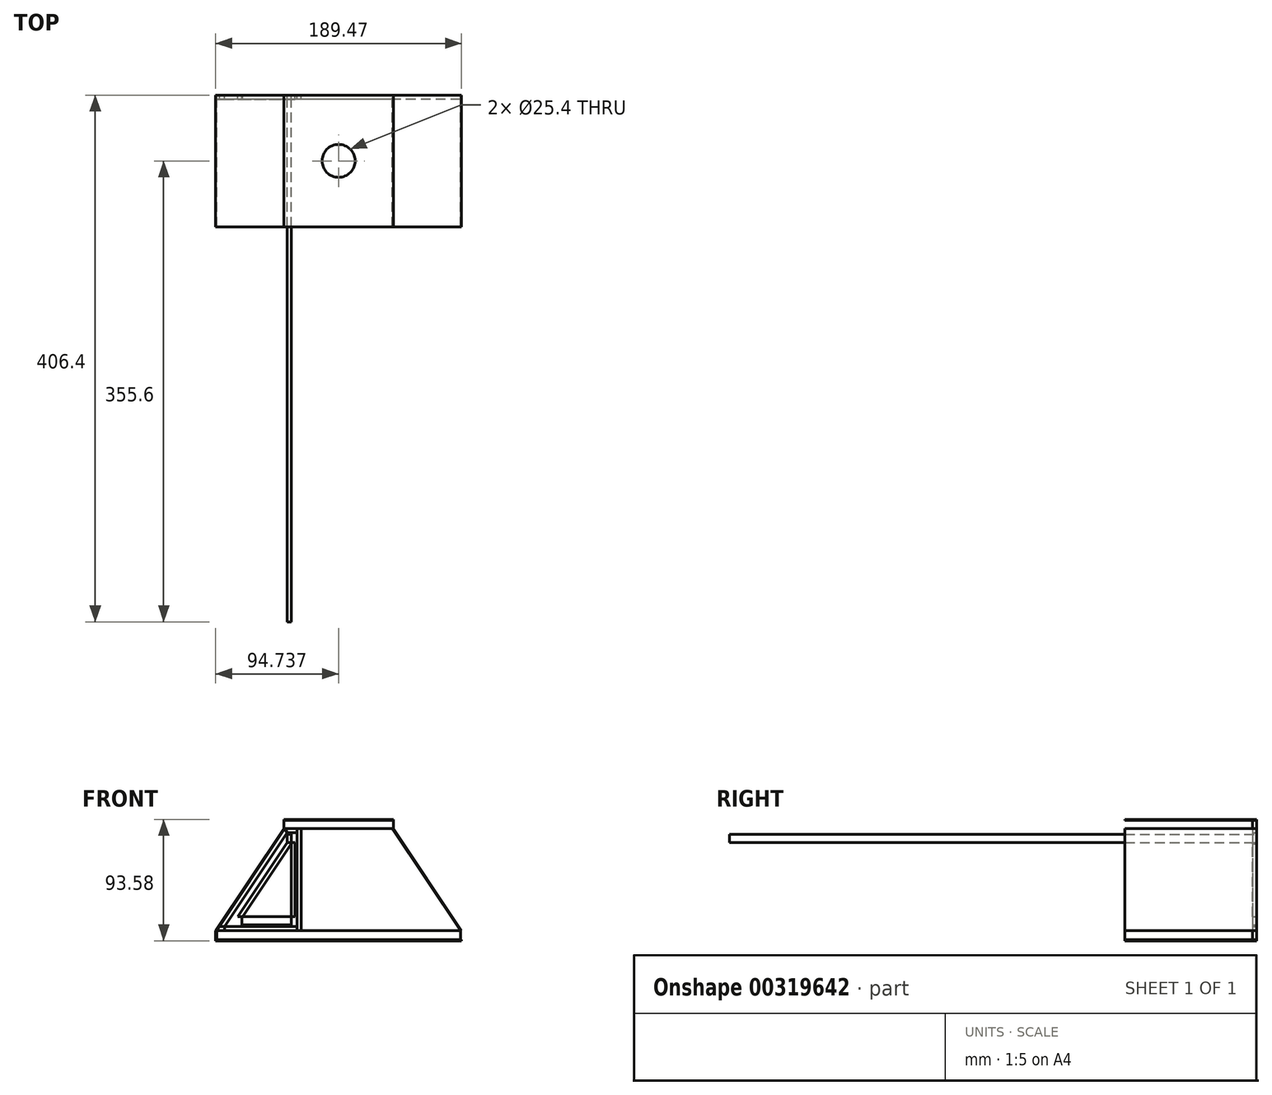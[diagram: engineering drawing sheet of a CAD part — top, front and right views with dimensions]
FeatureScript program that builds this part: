
annotation { "Feature Type Name" : "Feature", "Feature Type Description" : "" }
export const myFeature = defineFeature(function(context is Context, id is Id, definition is map)
    precondition{}
    {
        {
            var Q0;
            Q0=qCreatedBy(makeId("Front.planeOp"),FACE);
            var sketch = newSketch(context, id + "F0", { "sketchPlane" : qUnion([Q0])});
            skLineSegment(sketch, "E0", {"start": v(-44.45, 0) * mm, "end": v(0, 0) * mm});
            skLineSegment(sketch, "E1", {"start": v(0, 0) * mm, "end": v(0, 6.35) * mm});
            skLineSegment(sketch, "E2", {"start": v(-44.45, 6.35) * mm, "end": v(-44.45, 0) * mm});
            skLineSegment(sketch, "E3", {"start": v(-44.45, 6.35) * mm, "end": v(0, 6.35) * mm});
            skLineSegment(sketch, "E4", {"start": v(-41.28, 6.35) * mm, "end": v(-41.28, 0) * mm});
            skLineSegment(sketch, "E5", {"start": v(-3.17, 6.35) * mm, "end": v(-3.17, 0) * mm});
            skLineSegment(sketch, "E6", {"start": v(-3.18, 62.54) * mm, "end": v(-40.63, 6.35) * mm});
            skLineSegment(sketch, "E7", {"start": v(-3.18, 62.54) * mm, "end": v(-3.18, 6.35) * mm});
            skLineSegment(sketch, "E8", {"start": v(0, 6.35) * mm, "end": v(0, 63.5) * mm});
            skLineSegment(sketch, "E9", {"start": v(-6.35, 63.5) * mm, "end": v(-44.45, 6.35) * mm});
            skLineSegment(sketch, "E10", {"start": v(-6.35, 63.5) * mm, "end": v(0, 63.5) * mm});
            skLineSegment(sketch, "E11", {"start": v(0, 63.5) * mm, "end": v(0, 69.85) * mm});
            skLineSegment(sketch, "E12", {"start": v(0, 69.85) * mm, "end": v(-6.35, 69.85) * mm});
            skLineSegment(sketch, "E13", {"start": v(-6.35, 69.85) * mm, "end": v(-6.35, 63.5) * mm});
            skLineSegment(sketch, "E14", {"start": v(-3.18, 63.5) * mm, "end": v(-3.18, 69.85) * mm});
            skLineSegment(sketch, "E15", {"start": v(-3.18, 62.54) * mm, "end": v(-3.18, 63.5) * mm});
            skSolve(sketch);
        }
        {
            var Q0;
            {var subQ0=sQuery(id+"F0.wireOp",EDGE,"E13");Q0=makeQuery(id+"F0.imprint","IMPRINT",FACE,{"disambiguationData":[TD([[makeQuery(id+"F0.imprint","IMPRINT",EDGE,{"derivedFrom":subQ0}),1.0]])]});}
            extrude(context, id + "F1", {"entities" : qUnion([Q0]), "depth" : 406.4 * mm});
        }
        {
            var Q0;
            {var subQ4=sQuery(id+"F0.wireOp",EDGE,"E4");Q0=makeQuery(id+"F0.imprint","IMPRINT",FACE,{"disambiguationData":[TD([[makeQuery(id+"F0.imprint","IMPRINT",EDGE,{"derivedFrom":subQ4}),1.0]])]});}
            extrude(context, id + "F2", {"entities" : qUnion([Q0]), "depth" : 3.17 * mm});
        }
        {
            var Q0;
            {var subQ0=sQuery(id+"F0.wireOp",EDGE,"E6");Q0=makeQuery(id+"F0.imprint","IMPRINT",FACE,{"disambiguationData":[TD([[makeQuery(id+"F0.imprint","IMPRINT",EDGE,{"derivedFrom":subQ0}),-1.0]])]});}
            extrude(context, id + "F3", {"entities" : qUnion([Q0]), "depth" : 3.17 * mm});
        }
        {
            var Q0;
            {var subQ3=sQuery(id+"F0.wireOp",EDGE,"E7");Q0=makeQuery(id+"F0.imprint","IMPRINT",FACE,{"disambiguationData":[TD([[makeQuery(id+"F0.imprint","IMPRINT",EDGE,{"derivedFrom":subQ3}),1.0]])]});}
            extrude(context, id + "F4", {"entities" : qUnion([Q0]), "depth" : 3.17 * mm});
        }
        {
            var Q0;
            Q0=makeQuery(id+"F2.opExtrude","CAP_FACE",FACE,{"disambiguationData":[OSD([sQuery(id+"F0.wireOp",EDGE,"E0"),sQuery(id+"F0.wireOp",EDGE,"E3"),sQuery(id+"F0.wireOp",EDGE,"E4"),sQuery(id+"F0.wireOp",EDGE,"E5")])],"isStart":true});
            var sketch = newSketch(context, id + "F5", { "sketchPlane" : qUnion([Q0])});
            skLineSegment(sketch, "E16", {"start": v(-1.27, 71.12) * mm, "end": v(6.35, 71.12) * mm});
            skLineSegment(sketch, "E17", {"start": v(6.35, 71.12) * mm, "end": v(54.61, -1.27) * mm});
            skLineSegment(sketch, "E18", {"start": v(54.61, -1.27) * mm, "end": v(-1.27, -1.27) * mm});
            skLineSegment(sketch, "E19", {"start": v(-1.27, -1.27) * mm, "end": v(-1.27, 71.12) * mm});
            skLineSegment(sketch, "E20.0", {"start": v(8.05, 74.3) * mm, "end": v(60.54, -4.45) * mm});
            skLineSegment(sketch, "E20.1", {"start": v(-4.44, 74.3) * mm, "end": v(8.05, 74.3) * mm});
            skLineSegment(sketch, "E20.2", {"start": v(-4.45, -4.45) * mm, "end": v(-4.44, 74.3) * mm});
            skLineSegment(sketch, "E20.3", {"start": v(60.54, -4.45) * mm, "end": v(-4.45, -4.45) * mm});
            skLineSegment(sketch, "E21", {"start": v(-75.64, 74.3) * mm, "end": v(8.84, 74.3) * mm});
            skLineSegment(sketch, "E22", {"start": v(8.84, 74.3) * mm, "end": v(61.34, -4.44) * mm});
            skLineSegment(sketch, "E23", {"start": v(61.34, -4.45) * mm, "end": v(60.54, -4.45) * mm});
            skLineSegment(sketch, "E24", {"start": v(8.84, 74.3) * mm, "end": v(8.84, 80.39) * mm});
            skLineSegment(sketch, "E25", {"start": v(8.84, 80.39) * mm, "end": v(-75.64, 80.39) * mm});
            skLineSegment(sketch, "E26", {"start": v(61.34, -4.45) * mm, "end": v(61.34, -11.6) * mm});
            skLineSegment(sketch, "E27", {"start": v(61.34, -11.6) * mm, "end": v(-128.13, -11.6) * mm});
            skLineSegment(sketch, "E28", {"start": v(61.34, -11.6) * mm, "end": v(61.34, -12.4) * mm});
            skLineSegment(sketch, "E29", {"start": v(61.34, -12.4) * mm, "end": v(-128.13, -12.4) * mm});
            skLineSegment(sketch, "E30", {"start": v(-128.13, -11.6) * mm, "end": v(-128.13, -12.4) * mm});
            skLineSegment(sketch, "E31", {"start": v(-128.13, -11.6) * mm, "end": v(-128.13, -4.45) * mm});
            skLineSegment(sketch, "E32", {"start": v(-75.64, 74.3) * mm, "end": v(-128.13, -4.45) * mm});
            skLineSegment(sketch, "E33", {"start": v(-75.64, 74.3) * mm, "end": v(-75.64, 80.39) * mm});
            skLineSegment(sketch, "E34", {"start": v(-1.27, 71.12) * mm, "end": v(-1.27, 74.3) * mm});
            skLineSegment(sketch, "E35", {"start": v(-1.27, -1.27) * mm, "end": v(-1.27, -4.45) * mm});
            skLineSegment(sketch, "E36", {"start": v(54.61, -1.27) * mm, "end": v(58.43, -1.27) * mm});
            skLineSegment(sketch, "E37", {"start": v(54.61, -1.27) * mm, "end": v(54.61, -4.45) * mm});
            skLineSegment(sketch, "E38", {"start": v(-128.13, -4.45) * mm, "end": v(-4.45, -4.45) * mm});
            skLineSegment(sketch, "E39", {"start": v(8.05, 74.3) * mm, "end": v(6.35, 71.12) * mm});
            skLineSegment(sketch, "E40", {"start": v(-75.64, 80.39) * mm, "end": v(-75.64, 81.18) * mm});
            skLineSegment(sketch, "E41", {"start": v(8.84, 80.39) * mm, "end": v(8.84, 81.18) * mm});
            skLineSegment(sketch, "E42", {"start": v(8.84, 81.18) * mm, "end": v(-75.64, 81.18) * mm});
            skLineSegment(sketch, "E43", {"start": v(-33.4, -11.6) * mm, "end": v(-33.4, 81.18) * mm, "construction": true});
            skLineSegment(sketch, "E44", {"start": v(60.54, -4.45) * mm, "end": v(60.54, -11.6) * mm});
            skLineSegment(sketch, "E45", {"start": v(-127.34, -4.45) * mm, "end": v(-127.34, -11.6) * mm});
            skLineSegment(sketch, "E46", {"start": v(-127.34, -4.45) * mm, "end": v(-74.84, 74.3) * mm});
            skSolve(sketch);
        }
        {
            var Q0;
            {var subQ2=sQuery(id+"F5.wireOp",EDGE,"E24");Q0=makeQuery(id+"F5.imprint","IMPRINT",FACE,{"disambiguationData":[TD([[makeQuery(id+"F5.imprint","IMPRINT",EDGE,{"derivedFrom":subQ2}),1.0]])]});}
            extrude(context, id + "F6", {"entities" : qUnion([Q0]), "oppositeDirection" : true, "depth" : 3.17 * mm});
        }
        {
            var Q0;
            {var subQ3=sQuery(id+"F5.wireOp",EDGE,"E22");Q0=makeQuery(id+"F5.imprint","IMPRINT",FACE,{"disambiguationData":[TD([[makeQuery(id+"F5.imprint","IMPRINT",EDGE,{"derivedFrom":subQ3}),-1.0]])]});}
            extrude(context, id + "F7", {"entities" : qUnion([Q0]), "oppositeDirection" : true, "depth" : 101.6 * mm});
        }
        {
            var Q0;
            Q0=makeQuery(id+"F5.imprint","IMPRINT",FACE,{"disambiguationData":[TD([[makeQuery(id+"F5.imprint","IMPRINT",EDGE,{"derivedFrom":sQuery(id+"F5.wireOp",EDGE,"E16")}),1.0]])]});
            extrude(context, id + "F8", {"entities" : qUnion([Q0]), "oppositeDirection" : true, "depth" : 3.17 * mm});
        }
        {
            var Q0;
            Q0=makeQuery(id+"F5.imprint","IMPRINT",FACE,{"disambiguationData":[TD([[makeQuery(id+"F5.imprint","IMPRINT",EDGE,{"derivedFrom":sQuery(id+"F5.wireOp",EDGE,"E17")}),1.0]])]});
            extrude(context, id + "F9", {"entities" : qUnion([Q0]), "oppositeDirection" : true, "depth" : 3.17 * mm});
        }
        {
            var Q0;
            Q0=makeQuery(id+"F5.imprint","IMPRINT",FACE,{"disambiguationData":[TD([[makeQuery(id+"F5.imprint","IMPRINT",EDGE,{"derivedFrom":sQuery(id+"F5.wireOp",EDGE,"E19")}),1.0]])]});
            extrude(context, id + "F10", {"entities" : qUnion([Q0]), "oppositeDirection" : true, "depth" : 3.17 * mm});
        }
        {
            var Q0;
            {var subQ3=sQuery(id+"F5.wireOp",EDGE,"E36");Q0=makeQuery(id+"F5.imprint","IMPRINT",FACE,{"disambiguationData":[TD([[makeQuery(id+"F5.imprint","IMPRINT",EDGE,{"derivedFrom":subQ3}),-1.0]])]});}
            extrude(context, id + "F11", {"entities" : qUnion([Q0]), "oppositeDirection" : true, "depth" : 3.17 * mm});
        }
        {
            var Q0;
            Q0=makeQuery(id+"F5.imprint","IMPRINT",FACE,{"disambiguationData":[TD([[makeQuery(id+"F5.imprint","IMPRINT",EDGE,{"derivedFrom":sQuery(id+"F5.wireOp",EDGE,"E18")}),1.0]])]});
            extrude(context, id + "F12", {"entities" : qUnion([Q0]), "oppositeDirection" : true, "depth" : 3.17 * mm});
        }
        {
            var Q0;
            Q0=makeQuery(id+"F5.imprint","IMPRINT",FACE,{"disambiguationData":[TD([[makeQuery(id+"F5.imprint","IMPRINT",EDGE,{"derivedFrom":sQuery(id+"F5.wireOp",EDGE,"E27")}),1.0]])]});
            var Q1;
            Q1=makeQuery(id+"F5.imprint","IMPRINT",FACE,{"disambiguationData":[TD([[makeQuery(id+"F5.imprint","IMPRINT",EDGE,{"derivedFrom":sQuery(id+"F5.wireOp",EDGE,"E25")}),-1.0]])]});
            extrude(context, id + "F13", {"entities" : qUnion([Q0, Q1]), "oppositeDirection" : true, "depth" : 101.6 * mm});
        }
        {
            var Q0;
            Q0=makeQuery(id+"F13.opExtrude","SWEPT_FACE",FACE,{"disambiguationData":[OSD([sQuery(id+"F5.wireOp",EDGE,"E42")])]});
            var sketch = newSketch(context, id + "F14", { "sketchPlane" : qUnion([Q0])});
            skLineSegment(sketch, "E47", {"start": v(-8.84, 0) * mm, "end": v(75.64, -101.6) * mm, "construction": true});
            skCircle(sketch, "E48", {"center": v(33.4, -50.8) * mm, "radius": 12.7 * mm});
            skSolve(sketch);
        }
        {
            var Q0;
            Q0 = qSketchRegion(id + "F14", true);
            extrude(context, id + "F15", {"entities" : qUnion([Q0]), "operationType" : NewBodyOperationType.REMOVE, "endBound" : BoundingType.THROUGH_ALL, "oppositeDirection" : true, "depth" : 25.4 * mm});
        }
        {
            var Q0;
            {var subQ3=sQuery(id+"F5.wireOp",EDGE,"E22");Q0=makeQuery(id+"F5.imprint","IMPRINT",FACE,{"disambiguationData":[TD([[makeQuery(id+"F5.imprint","IMPRINT",EDGE,{"derivedFrom":subQ3}),-1.0]])]});}
            extrude(context, id + "F16", {"entities" : qUnion([Q0]), "oppositeDirection" : true, "depth" : 101.6 * mm});
        }
        {
            var Q0;
            Q0=makeQuery(id+"F5.imprint","IMPRINT",FACE,{"disambiguationData":[TD([[makeQuery(id+"F5.imprint","IMPRINT",EDGE,{"derivedFrom":sQuery(id+"F5.wireOp",EDGE,"E23")}),1.0]])]});
            extrude(context, id + "F17", {"entities" : qUnion([Q0]), "oppositeDirection" : true, "depth" : 101.6 * mm});
        }
        {
            var Q0;
            {var subQ0=sQuery(id+"F5.wireOp",EDGE,"E44");Q0=makeQuery(id+"F5.imprint","IMPRINT",FACE,{"disambiguationData":[TD([[makeQuery(id+"F5.imprint","IMPRINT",EDGE,{"derivedFrom":subQ0}),-1.0]])]});}
            extrude(context, id + "F18", {"entities" : qUnion([Q0]), "oppositeDirection" : true, "depth" : 3.17 * mm});
        }
        {
            var Q0;
            {var subQ0=sQuery(id+"F5.wireOp",EDGE,"E32");Q0=makeQuery(id+"F5.imprint","IMPRINT",FACE,{"disambiguationData":[TD([[makeQuery(id+"F5.imprint","IMPRINT",EDGE,{"derivedFrom":subQ0}),1.0]])]});}
            extrude(context, id + "F19", {"entities" : qUnion([Q0]), "oppositeDirection" : true, "depth" : 101.6 * mm});
        }
    });
